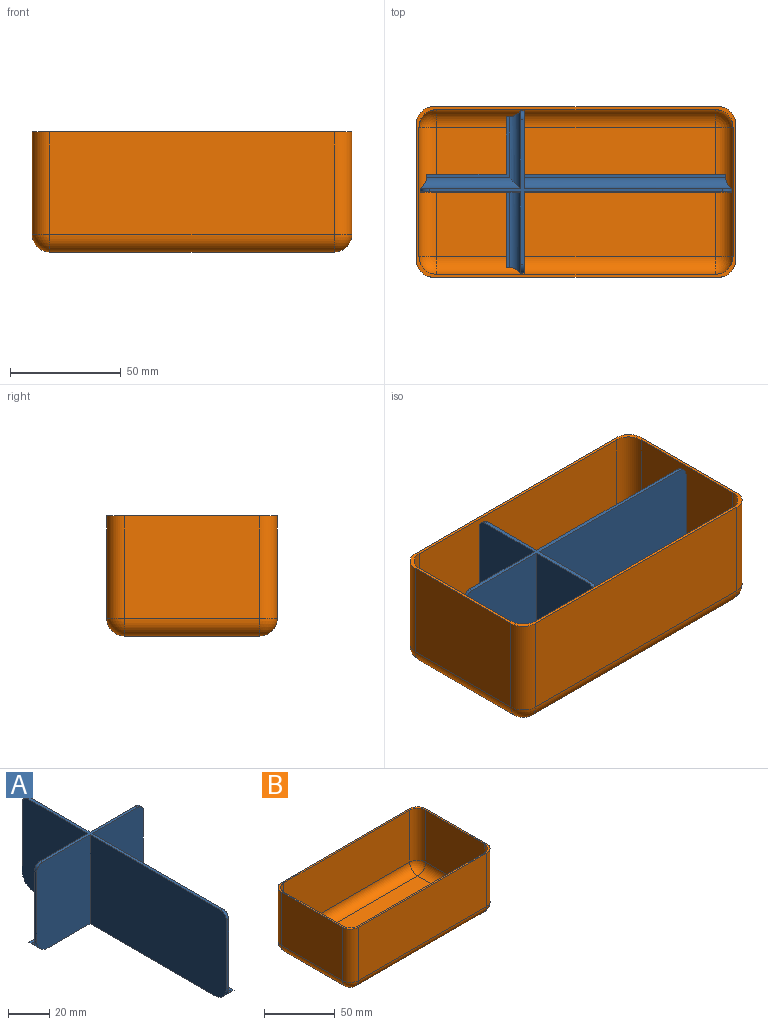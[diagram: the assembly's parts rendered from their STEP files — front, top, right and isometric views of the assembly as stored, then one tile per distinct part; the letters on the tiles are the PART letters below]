
ASSEMBLY  parts=2 mates=1
PART A: 33 faces, bbox 73.5x140.7x53 mm
  f0: plane 36.14x2mm, normal (1,0,0), area 69mm2, adj f7,f8,f17,f23
  f1: plane 91.14x2mm, normal (1,0,0), area 179mm2, adj f2,f7,f19,f24
  f2: plane 91.14x1.4mm, normal (0,0,1), area 127.6mm2, adj f1,f19,f24,f25
  f3: plane 46x45.25mm, normal (1,0,0), area 2078mm2, adj f9,f11,f18,f23,f26,f31
  f4: plane 93.85x46mm, normal (1,0,0), area 4313.6mm2, adj f9,f10,f19,f24,f25,f32
  f5: plane 53x45.25mm, normal (-1,0,0), area 2362.9mm2, adj f7,f9,f11,f13,f14,f15,f23,f28
  f6: plane 93.85x53mm, normal (-1,0,0), area 4956.9mm2, adj f7,f9,f10,f16,f24,f32
  f7: plane 124.7x57.5mm, normal (0,0,-1), area 1393.6mm2, adj f0,f1,f5,f6,f15,f16,f17,f19
  f8: plane 37.54x27.44mm, normal (0,0,1), area 89mm2, adj f0,f17,f22,f23,f26,f27
  f9: plane 132.7x65.5mm, normal (0,0,1), area 314.6mm2, adj f3,f4,f5,f6,f13,f16,f18,f19
  f10: plane 41x1.6mm, normal (0,-1,0), area 65.6mm2, adj f4,f6,f24,f32
  f11: plane 41x1.6mm, normal (0,1,0), area 65.6mm2, adj f3,f5,f23,f31
  f12: plane 41x1.6mm, normal (-1,0,0), area 65.6mm2, adj f13,f16,f21,f29
  f13: plane 46x36.75mm, normal (0,1,0), area 1687mm2, adj f5,f9,f12,f21,f28,f29
  f14: plane 34.04x1.4mm, normal (0,0,1), area 47.7mm2, adj f5,f15,f21,f28
  f15: plane 34.04x2mm, normal (0,1,0), area 64.8mm2, adj f5,f7,f14,f21
  f16: plane 53x36.75mm, normal (0,-1,0), area 1930.6mm2, adj f6,f7,f9,f12,f21,f29
  f17: plane 26.04x2mm, normal (0,1,0), area 48.8mm2, adj f0,f7,f8,f22
  f18: plane 46x35.15mm, normal (0,1,0), area 1613.4mm2, adj f3,f9,f20,f22,f27,f30
  f19: plane 53x35.15mm, normal (0,-1,0), area 1827.6mm2, adj f1,f2,f4,f7,f9,f20,f22,f25
  f20: plane 41x1.6mm, normal (1,0,0), area 65.6mm2, adj f18,f19,f22,f30
  f21: cylinder r=8mm len=8mm, axis (0,1,0), area 64.1mm2, adj f7,f12,f13,f14,f15,f16,f28
  f22: cylinder r=8mm len=8mm, axis (0,-1,0), area 64.1mm2, adj f7,f8,f17,f18,f19,f20,f27
  f23: cylinder r=8mm len=8mm, axis (1,0,0), area 64.1mm2, adj f0,f3,f5,f7,f8,f11,f26
  f24: cylinder r=8mm len=8mm, axis (-1,0,0), area 64.1mm2, adj f1,f2,f4,f6,f7,f10,f25
  f25: cylinder r=5mm len=93.79mm, axis (0,1,0), area 726mm2, adj f2,f4,f19,f24
  f26: cylinder r=5mm len=45.19mm, axis (0,1,0), area 330mm2, adj f3,f8,f23,f27
  f27: cylinder r=5mm len=35.09mm, axis (-1,0,0), area 250.7mm2, adj f8,f18,f22,f26
  f28: cylinder r=5mm len=36.69mm, axis (-1,0,0), area 277.5mm2, adj f5,f13,f14,f21
  f29: cylinder r=4mm len=4mm, axis (0,-1,0), area 10.1mm2, adj f9,f12,f13,f16
  f30: cylinder r=4mm len=4mm, axis (0,1,0), area 10.1mm2, adj f9,f18,f19,f20
  f31: cylinder r=4mm len=4mm, axis (-1,0,0), area 10.1mm2, adj f3,f5,f9,f11
  f32: cylinder r=4mm len=4mm, axis (1,0,0), area 10.1mm2, adj f4,f6,f9,f10
PART B: 35 faces, bbox 144.6x77.1x54.3 mm
  f0: plane 61.1x46.3mm, normal (1,0,0), area 2828.9mm2, adj f8,f13,f16,f26
  f1: plane 128.6x46.3mm, normal (0,1,0), area 5954.2mm2, adj f8,f13,f14,f22
  f2: plane 61.1x46.3mm, normal (-1,0,0), area 2828.9mm2, adj f8,f14,f15,f19
  f3: plane 58.5x45mm, normal (1,0,0), area 2632.5mm2, adj f8,f9,f12,f32
  f4: plane 126x45mm, normal (0,-1,0), area 5670mm2, adj f8,f9,f10,f28
  f5: plane 58.5x45mm, normal (-1,0,0), area 2632.5mm2, adj f8,f10,f11,f29
  f6: plane 126x45mm, normal (0,1,0), area 5670mm2, adj f8,f11,f12,f33
  f7: plane 128.6x46.3mm, normal (0,-1,0), area 5954.2mm2, adj f8,f15,f16,f23
  f8: plane 144.6x77.1mm, normal (0,0,1), area 569.7mm2, adj f0,f1,f2,f3,f4,f5,f6,f7
  f9: cylinder r=8mm len=45mm, axis (0,0,-1), area 565.5mm2, adj f3,f4,f8,f30
  f10: cylinder r=8mm len=45mm, axis (0,0,1), area 565.5mm2, adj f4,f5,f8,f27
  f11: cylinder r=8mm len=45mm, axis (0,0,-1), area 565.5mm2, adj f5,f6,f8,f31
  f12: cylinder r=8mm len=45mm, axis (0,0,1), area 565.5mm2, adj f3,f6,f8,f34
  f13: cylinder r=8mm len=46.3mm, axis (0,0,-1), area 581.8mm2, adj f0,f1,f8,f24
  f14: cylinder r=8mm len=46.3mm, axis (0,0,1), area 581.8mm2, adj f1,f2,f8,f20
  f15: cylinder r=8mm len=46.3mm, axis (0,0,-1), area 581.8mm2, adj f2,f7,f8,f21
  f16: cylinder r=8mm len=46.3mm, axis (0,0,1), area 581.8mm2, adj f0,f7,f8,f25
  f17: plane 126x58.5mm, normal (0,0,1), area 7371mm2, adj f28,f29,f32,f33
  f18: plane 128.6x61.1mm, normal (0,0,-1), area 7857.5mm2, adj f19,f22,f23,f26
  f19: cylinder r=8mm len=61.1mm, axis (0,-1,0), area 767.8mm2, adj f2,f18,f20,f21
  f20: sphere r=8mm, area 100.5mm2, adj f14,f19,f22
  f21: sphere r=8mm, area 100.5mm2, adj f15,f19,f23
  f22: cylinder r=8mm len=128.6mm, axis (-1,0,0), area 1616mm2, adj f1,f18,f20,f24
  f23: cylinder r=8mm len=128.6mm, axis (1,0,0), area 1616mm2, adj f7,f18,f21,f25
  f24: sphere r=8mm, area 100.5mm2, adj f13,f22,f26
  f25: sphere r=8mm, area 100.5mm2, adj f16,f23,f26
  f26: cylinder r=8mm len=61.1mm, axis (0,1,0), area 767.8mm2, adj f0,f18,f24,f25
  f27: sphere r=8mm, area 100.5mm2, adj f10,f28,f29
  f28: cylinder r=8mm len=126mm, axis (1,0,0), area 1583.4mm2, adj f4,f17,f27,f30
  f29: cylinder r=8mm len=58.5mm, axis (0,-1,0), area 735.1mm2, adj f5,f17,f27,f31
  f30: sphere r=8mm, area 100.5mm2, adj f9,f28,f32
  f31: sphere r=8mm, area 100.5mm2, adj f11,f29,f33
  f32: cylinder r=8mm len=58.5mm, axis (0,1,0), area 735.1mm2, adj f3,f17,f30,f34
  f33: cylinder r=8mm len=126mm, axis (-1,0,0), area 1583.4mm2, adj f6,f17,f31,f34
  f34: sphere r=8mm, area 100.5mm2, adj f12,f32,f33
PLACE A rot(axis=(0,0,1),90deg) t=(1.07,17.8,-0.08)mm
PLACE B t=(1.07,17.8,-0.08)mm
MATE revolute A.f7 <-> B.f17  axis (0,0,1) through (1.07,17.8,-0.08)mm
